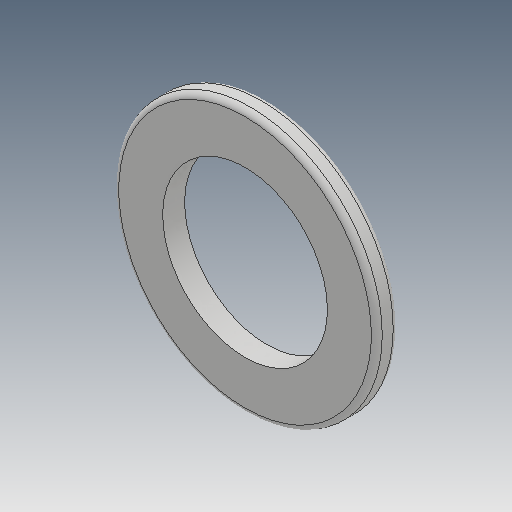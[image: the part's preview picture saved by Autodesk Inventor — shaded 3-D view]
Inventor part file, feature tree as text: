
AUTODESK INVENTOR PART (.ipt)
format: ipt  version: 2018 (Build 220112000, 112)  size: 108,544 bytes
history: native  units: mm
features: fillet x1
ambient origin geometry x8: Origin, YZ Plane, XZ Plane, XY Plane, X Axis, Y Axis, Z Axis, Center Point
bodies: Volumenkörper1 (feature_tree)
feature tree (1):
  fillet  "Fillet1"  [1 undecoded]
note: 1 required parameter value undecoded (feature->parameter linkage not recoverable at this tier; creation-order binding heuristic only, values carry confidence <= 0.55)
